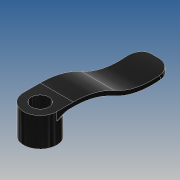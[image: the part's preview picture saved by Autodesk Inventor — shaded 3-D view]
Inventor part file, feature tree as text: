
AUTODESK INVENTOR PART (.ipt)
format: ipt  version: 2017 (Build 210142000, 142)  size: 251,904 bytes
history: native  units: mm
features: extrude x3, sketch x3, fillet x2, projected_geometry x1
ambient origin geometry x8: Origin, YZ Plane, XZ Plane, XY Plane, X Axis, Y Axis, Z Axis, Center Point
bodies: Solid1 (feature_tree)
feature tree (9):
  extrude  "Extrusion1"  Depth=8.0mm
  extrude  "PartieFlexible rayon 15 au lieu de 19.5"  Depth=19.5mm
  extrude  "Extrusion3"  Depth=1.0mm
  fillet  "Fillet1"  Radius=1.0mm
  fillet  "Fillet2"  Radius=8.0mm
  sketch  "Sketch1"  dims[d0=4.2mm d1=8.0mm]
  sketch  "Sketch2"  dims[d2=6.0mm d3=0.0mm d4=19.5mm]
  sketch  "Sketch3"  dims[d5=19.5mm d6=23.0mm d7=1.0mm d9=8.0mm d10=0.0mm d11=8.0mm d12=0.0mm d13=3.0mm d14=15.0deg d15=1.0mm]
  projected_geometry  "Project Cut Edges1"
